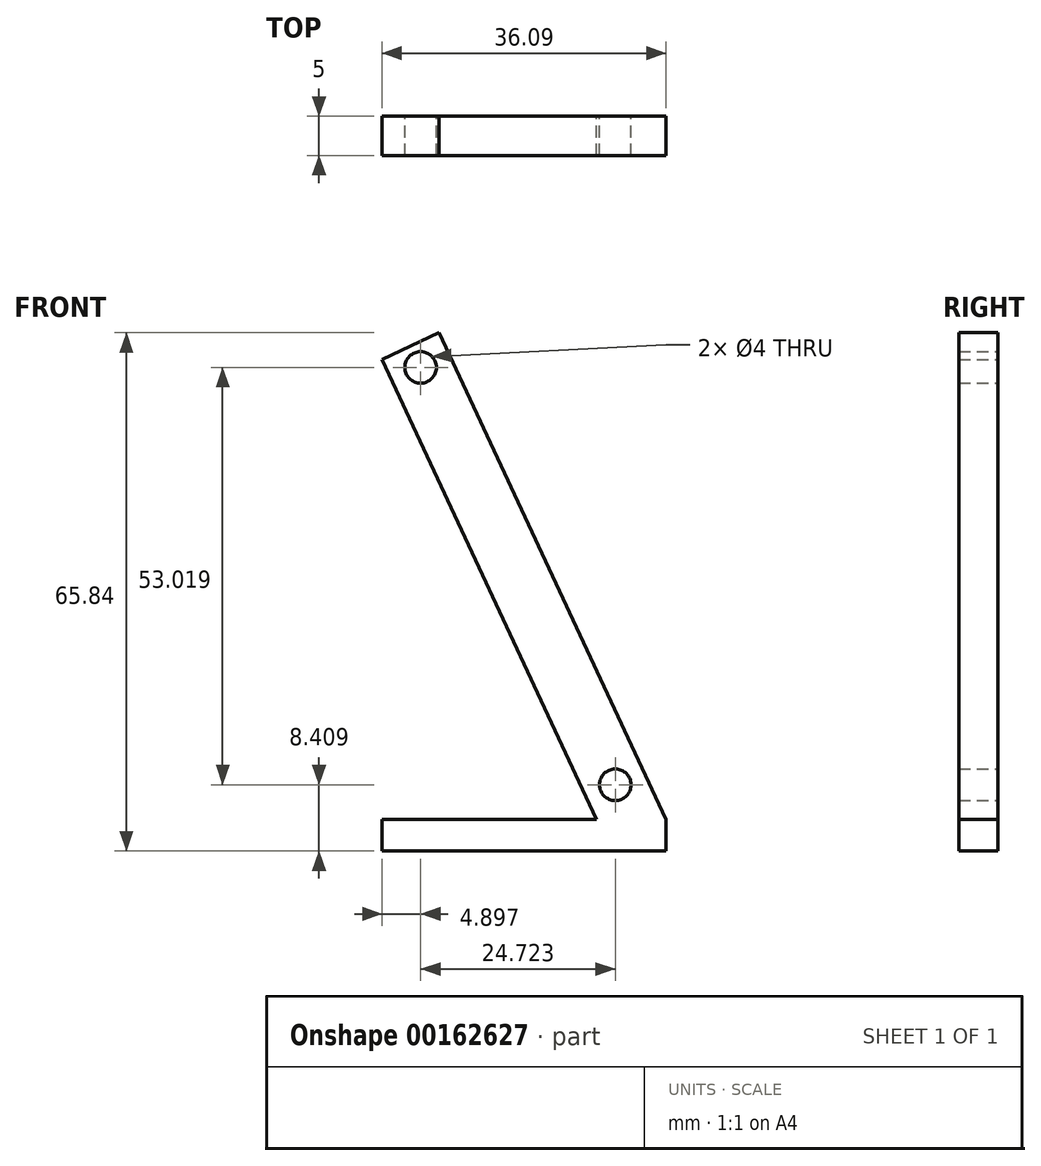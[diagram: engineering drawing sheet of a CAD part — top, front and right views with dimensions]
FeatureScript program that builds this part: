
annotation { "Feature Type Name" : "Feature", "Feature Type Description" : "" }
export const myFeature = defineFeature(function(context is Context, id is Id, definition is map)
    precondition{}
    {
        {
            var Q0;
            Q0=qCreatedBy(makeId("Front.planeOp"),FACE);
            var sketch = newSketch(context, id + "F0", { "sketchPlane" : qUnion([Q0])});
            skLineSegment(sketch, "E0", {"start": v(-36.09, 0) * mm, "end": v(-36.09, -4) * mm});
            skLineSegment(sketch, "E1", {"start": v(-36.09, -4) * mm, "end": v(0, -4) * mm});
            skLineSegment(sketch, "E2", {"start": v(-36.09, 0) * mm, "end": v(-8.83, 0) * mm});
            skLineSegment(sketch, "E3", {"start": v(-8.83, 0) * mm, "end": v(-36.09, 58.46) * mm});
            skLineSegment(sketch, "E4", {"start": v(0, -4) * mm, "end": v(0, 0) * mm});
            skLineSegment(sketch, "E5", {"start": v(0, 0) * mm, "end": v(-28.84, 61.84) * mm});
            skCircle(sketch, "E6", {"center": v(-31.2, 57.43) * mm, "radius": 2 * mm});
            skCircle(sketch, "E7", {"center": v(-6.47, 4.4) * mm, "radius": 2 * mm});
            skLineSegment(sketch, "E8", {"start": v(-31.2, 57.43) * mm, "end": v(-30.35, 55.62) * mm, "construction": true});
            skLineSegment(sketch, "E9", {"start": v(-7.31, 6.22) * mm, "end": v(-6.47, 4.4) * mm, "construction": true});
            skLineSegment(sketch, "E10", {"start": v(-30.35, 55.62) * mm, "end": v(-7.31, 6.22) * mm, "construction": true});
            skPoint(sketch, "E11", {"position": v(-18.83, 30.92) * mm});
            skPoint(sketch, "E12", {"position": v(-14.42, 30.92) * mm});
            skLineSegment(sketch, "E13", {"start": v(-22.46, 29.23) * mm, "end": v(-15.2, 32.6) * mm});
            skLineSegment(sketch, "E14", {"start": v(-28.84, 61.84) * mm, "end": v(-36.09, 58.46) * mm});
            skSolve(sketch);
        }
        {
            var Q0;
            Q0=makeQuery(id+"F0.imprint","IMPRINT",FACE,{"disambiguationData":[TD([[makeQuery(id+"F0.imprint","IMPRINT",EDGE,{"derivedFrom":sQuery(id+"F0.wireOp",EDGE,"E0")}),1.0]])]});
            var Q1;
            {var subQ0=sQuery(id+"F0.wireOp",EDGE,"GJgerAxX-R8nG-dXGn-GZzQ-9MWBVnkP7MwR");Q1=makeQuery(id+"F0.imprint","IMPRINT",FACE,{"disambiguationData":[TD([[makeQuery(id+"F0.imprint","IMPRINT",EDGE,{"derivedFrom":subQ0}),-1.0]])]});}
            var Q2;
            Q2=makeQuery(id+"F0.imprint","IMPRINT",FACE,{"disambiguationData":[TD([[makeQuery(id+"F0.imprint","IMPRINT",EDGE,{"derivedFrom":sQuery(id+"F0.wireOp",EDGE,"E6")}),-1.0]])]});
            extrude(context, id + "F1", {"entities" : qUnion([Q0, Q1, Q2]), "depth" : 5 * mm});
        }
    });
